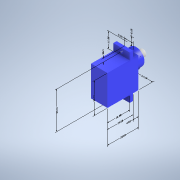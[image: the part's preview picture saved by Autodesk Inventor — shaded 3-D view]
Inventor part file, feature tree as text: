
AUTODESK INVENTOR PART (.ipt)
format: ipt  version: 2022.1 (Build 261234000, 234)  size: 215,040 bytes
history: native  units: mm
features: other x14, extrude x6, sketch x6
ambient origin geometry x8: Origin, YZ Plane, XZ Plane, XY Plane, X Axis, Y Axis, Z Axis, Center Point
bodies: Body1 (feature_tree)
feature tree (26):
  other  "Annotations"
  extrude  "Extrusion3"  Depth=32.5mm
  extrude  "Extrusion4"  Depth=22.5mm
  extrude  "Extrusion5"  Depth=16.5mm TaperAngle=0.0deg
  extrude  "Extrusion6"  Depth=2.5mm
  extrude  "Extrusion7"  Depth=2.5mm
  extrude  "Extrusion8"  Depth=6.1mm
  sketch  "Sketch3"  dims[d11=12.2mm d12=32.5mm]
  sketch  "Sketch4"  dims[d13=2.5mm d14=0.0mm d15=22.5mm]
  sketch  "Sketch5"  dims[d16=5.0mm d17=16.5mm d18=0.0mm]
  sketch  "Sketch6"  dims[d19=4.0mm d20=0.0mm d21=2.5mm]
  sketch  "Sketch7"  dims[d22=2.5mm d23=2.5mm]
  sketch  "Sketch8"  dims[d24=2.5mm d25=6.1mm d26=6.1mm d27=4.0mm d28=0.0mm d29=6.1mm d30=12.2mm d31=4.5mm d32=0.0mm d33=5.6mm d34=11.0mm d35=5.0mm d36=5.0mm d37=0.0mm d38=0.0mm d39=10.0mm d40=16.5mm d41=0.0mm d42=10.0mm d43=22.5mm d44=0.0mm d45=10.0mm d46=4.0mm d47=8.43141mm d48=1.60565mm d49=23.0mm d50=1.017257mm d51=3.928971mm d52=19.0mm d53=1.377897mm d54=27.5mm d55=1.068526mm d56=4.291887mm d57=6.1mm d58=2.750106mm d59=1.378855mm d60=2.5mm d63=0.0mm d64=10.0mm d65=12.2mm d66=11.8909mm d67=6.732525mm d68=7.629808mm d69=6.1mm d70=50.157306mm d71=2.8mm d72=11.5mm d73=6.1mm]
  other  "Linear Dimension 1"
  other  "Linear Dimension 2"
  other  "Linear Dimension 3"
  other  "Linear Dimension 4"
  other  "Linear Dimension 5"
  other  "Linear Dimension 6"
  other  "Linear Dimension 7"
  other  "Linear Dimension 8"
  other  "Linear Dimension 10"
  other  "Radial Dimension 1"
  other  "Radial Dimension 2"
  other  "Linear Dimension 11"
  other  "Linear Dimension 12"
